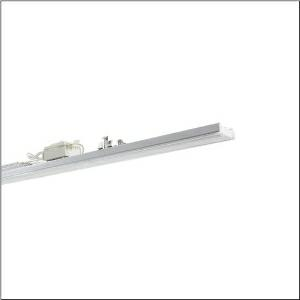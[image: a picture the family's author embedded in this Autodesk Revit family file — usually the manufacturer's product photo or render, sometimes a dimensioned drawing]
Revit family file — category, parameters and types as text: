
# Revit family: licross_r__11_recessed_mo_51tl12dn4axg3s4_5beb
name_source: partatom
category: Lighting Fixtures
units: mm (PartAtom-declared; Revit-internal decimal feet)

## family parameters
Cut with Voids When Loaded = No
Host = Face
Light Source = No
Part Type = Normal
Room Calculation Point = No
Round Connector Dimension = Use Diameter
Shared = No

## types (1)
- --- (1 x LED, 1010 lm, 6.7 W, 4000K)
    Apparent Load = 7 VA
    CIE Flux Codes = 67 92 99 100 100
    Color Rendering = 80
    Color Temperature = 4000K
    Default Elevation = 1800 mm
    Description = Licross® 11 Recessed MO, luminaire insert, of sheet steel, coil coated, white, length: 1.500mm, width: 66mm, height: 67mm, LED rated luminous flux: 10.240lm, light colour: 840, control gear: DALI 2, with plug, 6-pole, with phase selection, for trunking rail, 9 or 11-core, mains connection: 220..240V, AC, 50/60Hz, rated input power: 61W, for trunking rail, 9-/11-core, halogen-free wiring, for emergency light function, converter,control gear: single battery element, battery: LiFePO4, 9Ah, primary optical cover: cover, of PMMA, light emission: direct distribution, primary light characteristic: symmetric, protection rating (complete): IP40, insulation class (complete): insulation class I (protective earthing), certification: CE, UKCA, protection symbol: D if used in an environment without relevant dust loads with corresponding accessories, impact resistance: IK06, permissible ambient temperature for indoor applications: +5..+35°C, standard: EN 60598-2-22, LABS conformity tested according to VDMA 24364:2018-05, reducing of maximum allowable ambient temperature of 5°C with ceiling mounting, corresponds to IFS (International Featured Standards) requirements for safety and quality in the food industry, packaging unit: 1 piece
    Height = 58 mm
    Lamp = 1 x LED
    Lamp Light Flux = 1010 lm
    Lamp Power = 6.7 W
    Lamp count = 1
    Length = 1500 mm
    Luminous efficacy = 151 lm/W
    Manufacturer = Siteco
    ModVariant = No
    Model = 51TL12DN4AXG3S4
    Mounting Place = Ceiling
    Mounting Type = Pendant
    Number of Poles = 1
    OnlyDefault = Yes
    Power Factor = 1
    Product Name = Licross® 11 Recessed MO
    Product group = luminaire insert
    ProductGroupID = 902
    Protection Class = Protection class I
    Protection Degree = IP 40
    RLX_Detail_Level = 1
    RLX_Emergency_Light_Flux = 0 lm
    RLX_Emergency_Type = 0
    RLX_Emergency_Type_DB = No
    RlxData = <blob elided: 24737 chars, md5=0592a114>
    Socket = socket
    Standby Power = 0 W
    System Light Flux = 1010 lm
    System Power = 7 W
    Type Comments = : emergency light operation: 3 h
    Type Image = l_1296930.jpg
    URL = http://relux.com
    VarID = @adj_090090
    Voltage = 0 V
    Weight = 0.00 kg
    Width = 66 mm

## geometry (parser evidence)
native form markers: Blend x4, Sweep x11
no freeform markers — native parametric forms only
